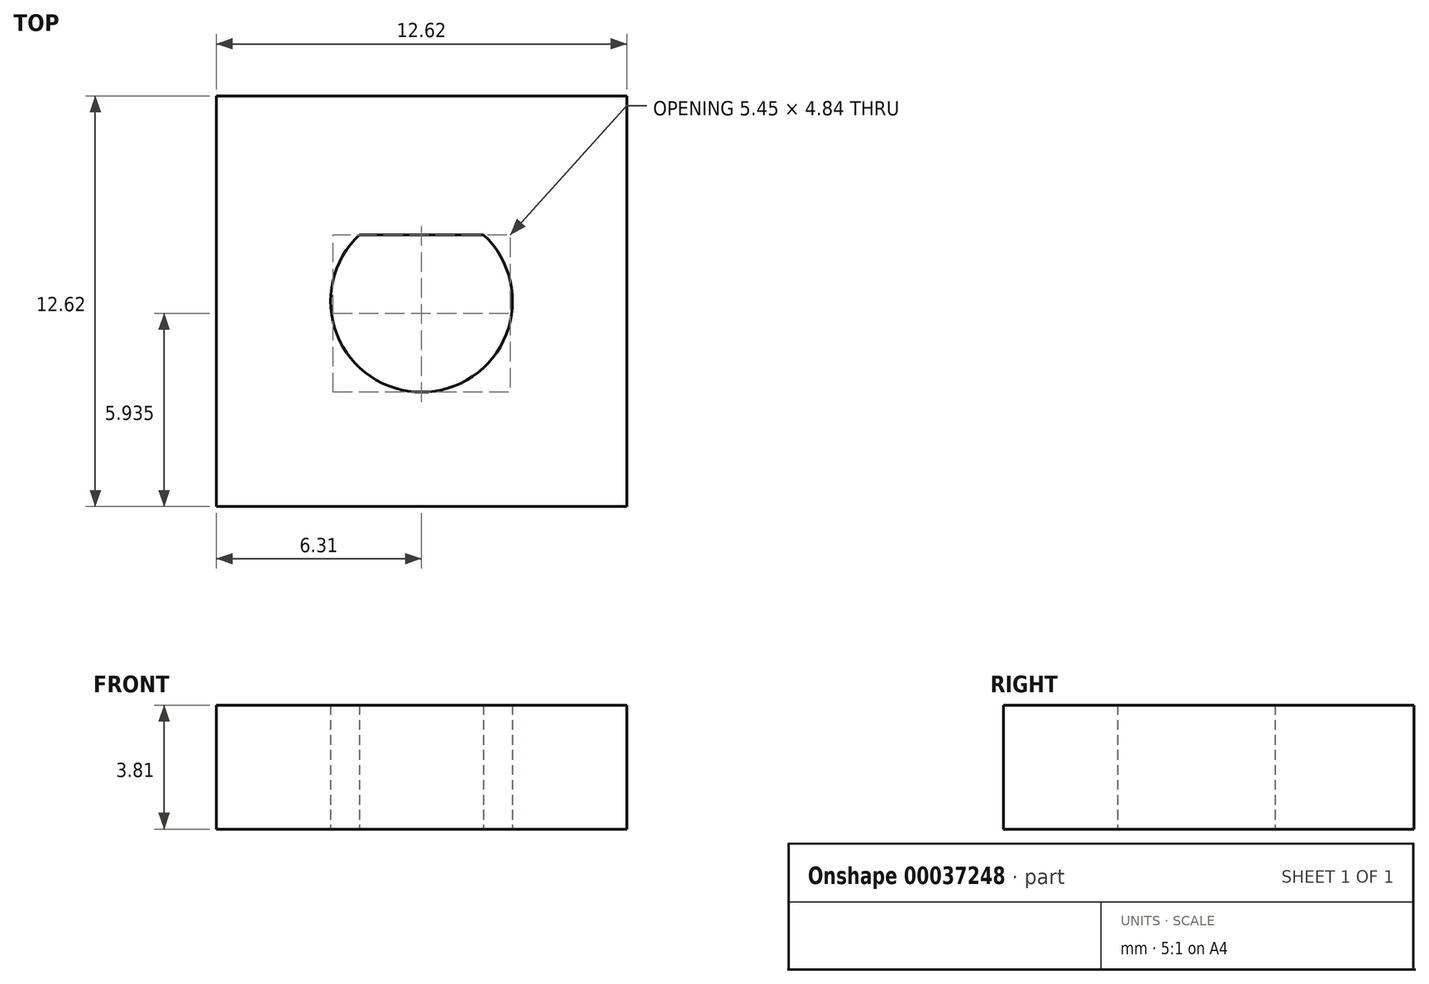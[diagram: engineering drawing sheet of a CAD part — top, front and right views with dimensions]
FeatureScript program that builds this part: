
annotation { "Feature Type Name" : "Feature", "Feature Type Description" : "" }
export const myFeature = defineFeature(function(context is Context, id is Id, definition is map)
    precondition{}
    {
        {
            var Q0;
            Q0=qCreatedBy(makeId("Top.planeOp"),FACE);
            var sketch = newSketch(context, id + "F0", { "sketchPlane" : qUnion([Q0])});
            skLineSegment(sketch, "E0.rect.bottom", {"start": v(6.3, 6.3) * mm, "end": v(-6.3, 6.3) * mm});
            skLineSegment(sketch, "E0.rect.top", {"start": v(6.3, -6.3) * mm, "end": v(-6.3, -6.3) * mm});
            skLineSegment(sketch, "E0.rect.left", {"start": v(6.3, 6.3) * mm, "end": v(6.3, -6.3) * mm});
            skLineSegment(sketch, "E0.rect.right", {"start": v(-6.3, 6.3) * mm, "end": v(-6.3, -6.3) * mm});
            skPoint(sketch, "E0.rect.middle", {"position": v(0, 0) * mm});
            skCircle(sketch, "E1", {"center": v(0, 0) * mm, "radius": 2.8 * mm});
            skLineSegment(sketch, "E2.rect.bottom", {"start": v(-1.9, 2.04) * mm, "end": v(1.9, 2.04) * mm});
            skLineSegment(sketch, "E2.rect.top", {"start": v(-1.9, -2.04) * mm, "end": v(1.9, -2.04) * mm});
            skLineSegment(sketch, "E2.rect.left", {"start": v(-1.9, 2.04) * mm, "end": v(-1.9, -2.04) * mm});
            skLineSegment(sketch, "E2.rect.right", {"start": v(1.9, 2.04) * mm, "end": v(1.9, -2.04) * mm});
            skSolve(sketch);
        }
        {
            var Q0;
            Q0=makeQuery(id+"F0.imprint","IMPRINT",FACE,{"disambiguationData":[TD([[makeQuery(id+"F0.imprint","IMPRINT",EDGE,{"derivedFrom":sQuery(id+"F0.wireOp",EDGE,"E0.rect.bottom")}),1.0]])]});
            var Q1;
            {var subQ0=sQuery(id+"F0.wireOp",EDGE,"E2.rect.bottom");Q1=makeQuery(id+"F0.imprint","IMPRINT",FACE,{"disambiguationData":[TD([[makeQuery(id+"F0.imprint","IMPRINT",EDGE,{"derivedFrom":subQ0}),1.0]])]});}
            extrude(context, id + "F1", {"entities" : qUnion([Q0, Q1]), "depth" : 3.8 * mm});
        }
    });
